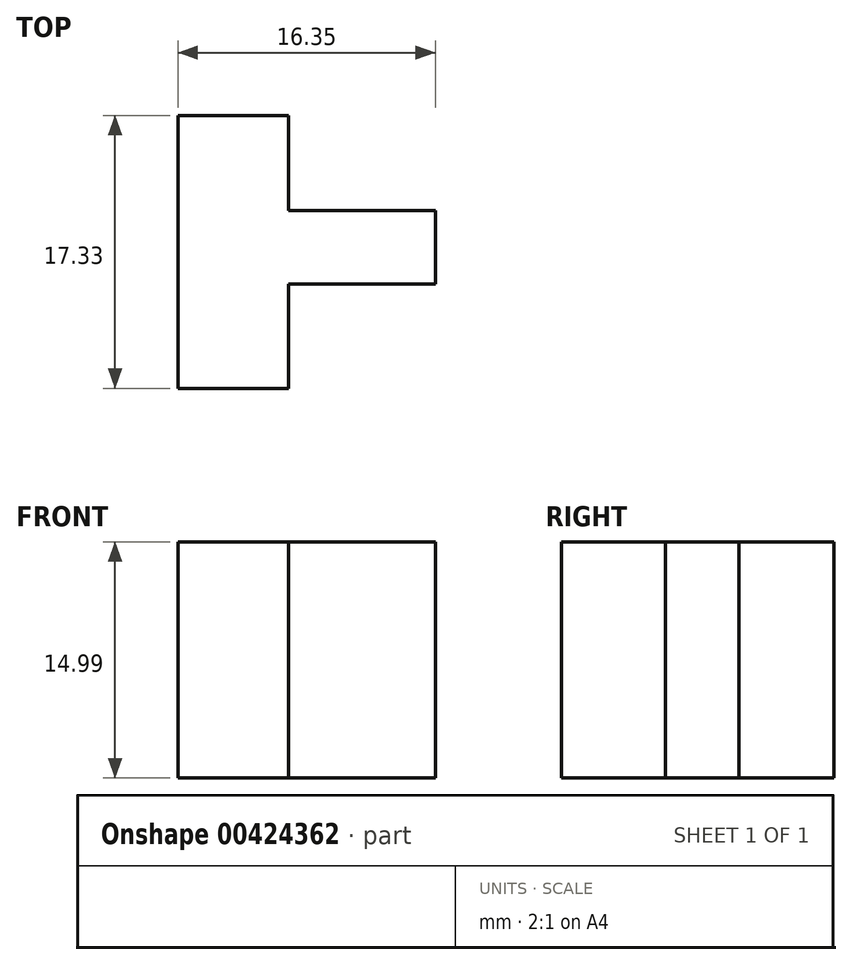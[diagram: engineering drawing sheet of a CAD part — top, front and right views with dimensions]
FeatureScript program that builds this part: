
annotation { "Feature Type Name" : "Feature", "Feature Type Description" : "" }
export const myFeature = defineFeature(function(context is Context, id is Id, definition is map)
    precondition{}
    {
        {
            var Q0;
            Q0=qCreatedBy(makeId("Top.planeOp"),FACE);
            var sketch = newSketch(context, id + "F0", { "sketchPlane" : qUnion([Q0])});
            skLineSegment(sketch, "E0", {"start": v(0, 0) * mm, "end": v(0, 17.33) * mm});
            skLineSegment(sketch, "E1", {"start": v(0, 17.33) * mm, "end": v(7, 17.33) * mm});
            skLineSegment(sketch, "E2", {"start": v(7, 17.33) * mm, "end": v(7, 11.3) * mm});
            skLineSegment(sketch, "E3", {"start": v(7, 11.3) * mm, "end": v(16.35, 11.3) * mm});
            skLineSegment(sketch, "E4", {"start": v(16.35, 11.3) * mm, "end": v(16.35, 6.62) * mm});
            skLineSegment(sketch, "E5", {"start": v(16.35, 6.62) * mm, "end": v(7, 6.62) * mm});
            skLineSegment(sketch, "E6", {"start": v(7, 6.62) * mm, "end": v(7, 0) * mm});
            skLineSegment(sketch, "E7", {"start": v(7, 0) * mm, "end": v(0, 0) * mm});
            skLineSegment(sketch, "E8", {"start": v(0, 17.33) * mm, "end": v(0, 1.75) * mm});
            skSolve(sketch);
        }
        {
            var Q0;
            Q0=makeQuery(id+"F0.imprint","IMPRINT",FACE,{"disambiguationData":[TD([[makeQuery(id+"F0.imprint","IMPRINT",EDGE,{"derivedFrom":sQuery(id+"F0.wireOp",EDGE,"E0")}),-1.0]])]});
            extrude(context, id + "F1", {"entities" : qUnion([Q0]), "depth" : 15 * mm});
        }
    });
